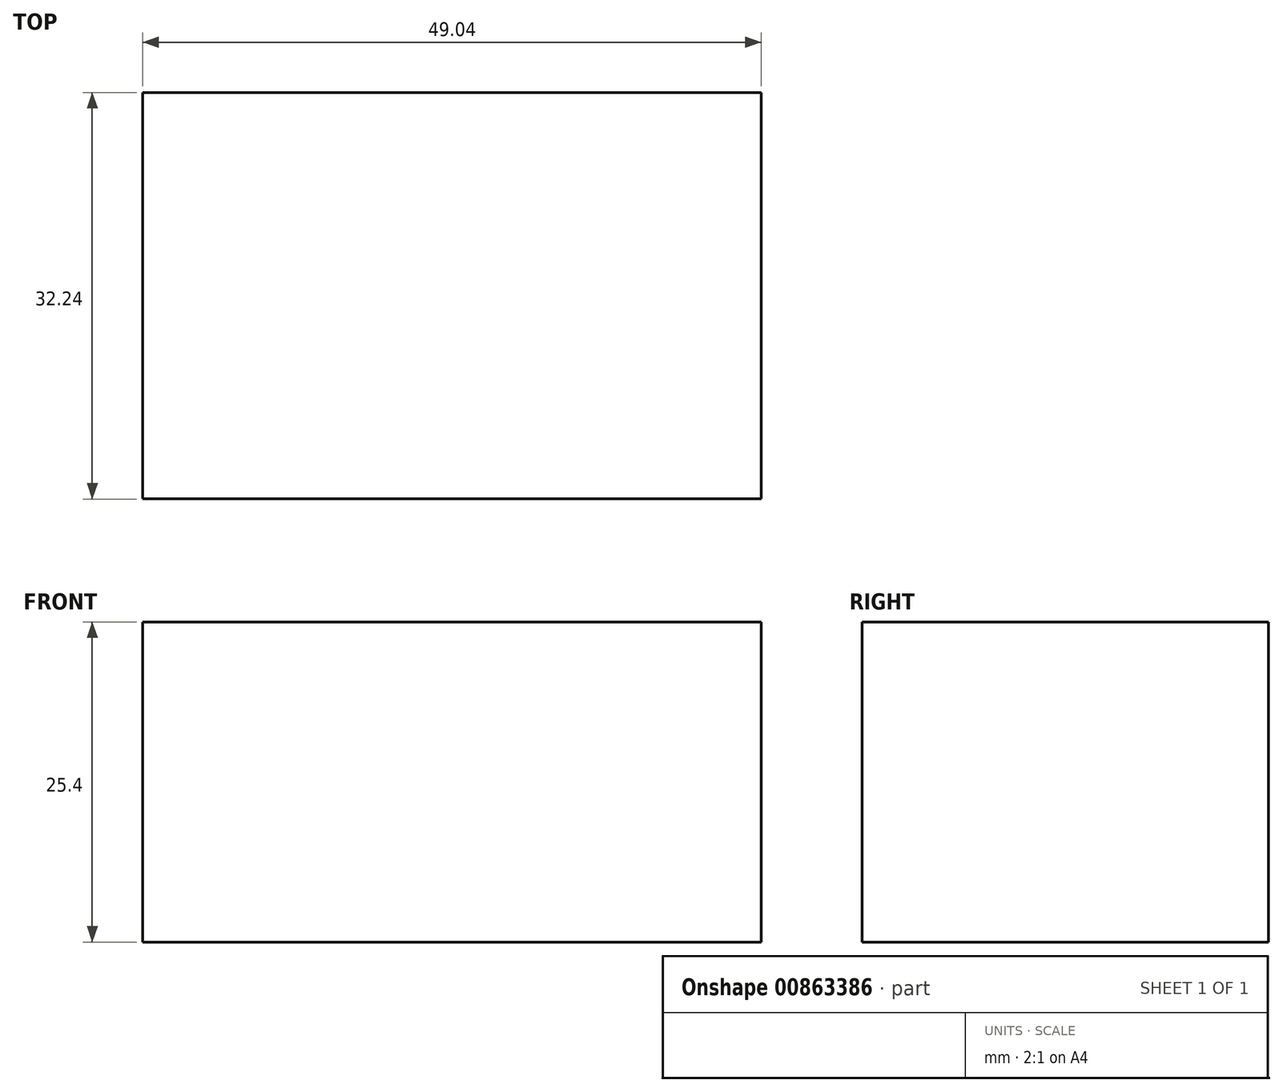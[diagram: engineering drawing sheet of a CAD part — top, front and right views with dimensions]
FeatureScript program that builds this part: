
annotation { "Feature Type Name" : "Feature", "Feature Type Description" : "" }
export const myFeature = defineFeature(function(context is Context, id is Id, definition is map)
    precondition{}
    {
        {
            var Q0;
            Q0=qCreatedBy(makeId("Top.planeOp"),FACE);
            var sketch = newSketch(context, id + "F0", { "sketchPlane" : qUnion([Q0])});
            skLineSegment(sketch, "E0.bottom", {"start": v(0, 0) * mm, "end": v(49.04, 0) * mm});
            skLineSegment(sketch, "E0.top", {"start": v(0, -32.24) * mm, "end": v(49.04, -32.24) * mm});
            skLineSegment(sketch, "E0.left", {"start": v(0, 0) * mm, "end": v(0, -32.24) * mm});
            skLineSegment(sketch, "E0.right", {"start": v(49.04, 0) * mm, "end": v(49.04, -32.24) * mm});
            skSolve(sketch);
        }
        {
            var Q0;
            Q0=makeQuery(id+"F0.imprint","IMPRINT",FACE,{"disambiguationData":[TD([[makeQuery(id+"F0.imprint","IMPRINT",EDGE,{"derivedFrom":sQuery(id+"F0.wireOp",EDGE,"E0.bottom")}),-1.0]])]});
            extrude(context, id + "F1", {"entities" : qUnion([Q0]), "depth" : 25.4 * mm, "offsetDistance" : 25.4 * mm});
        }
    });
